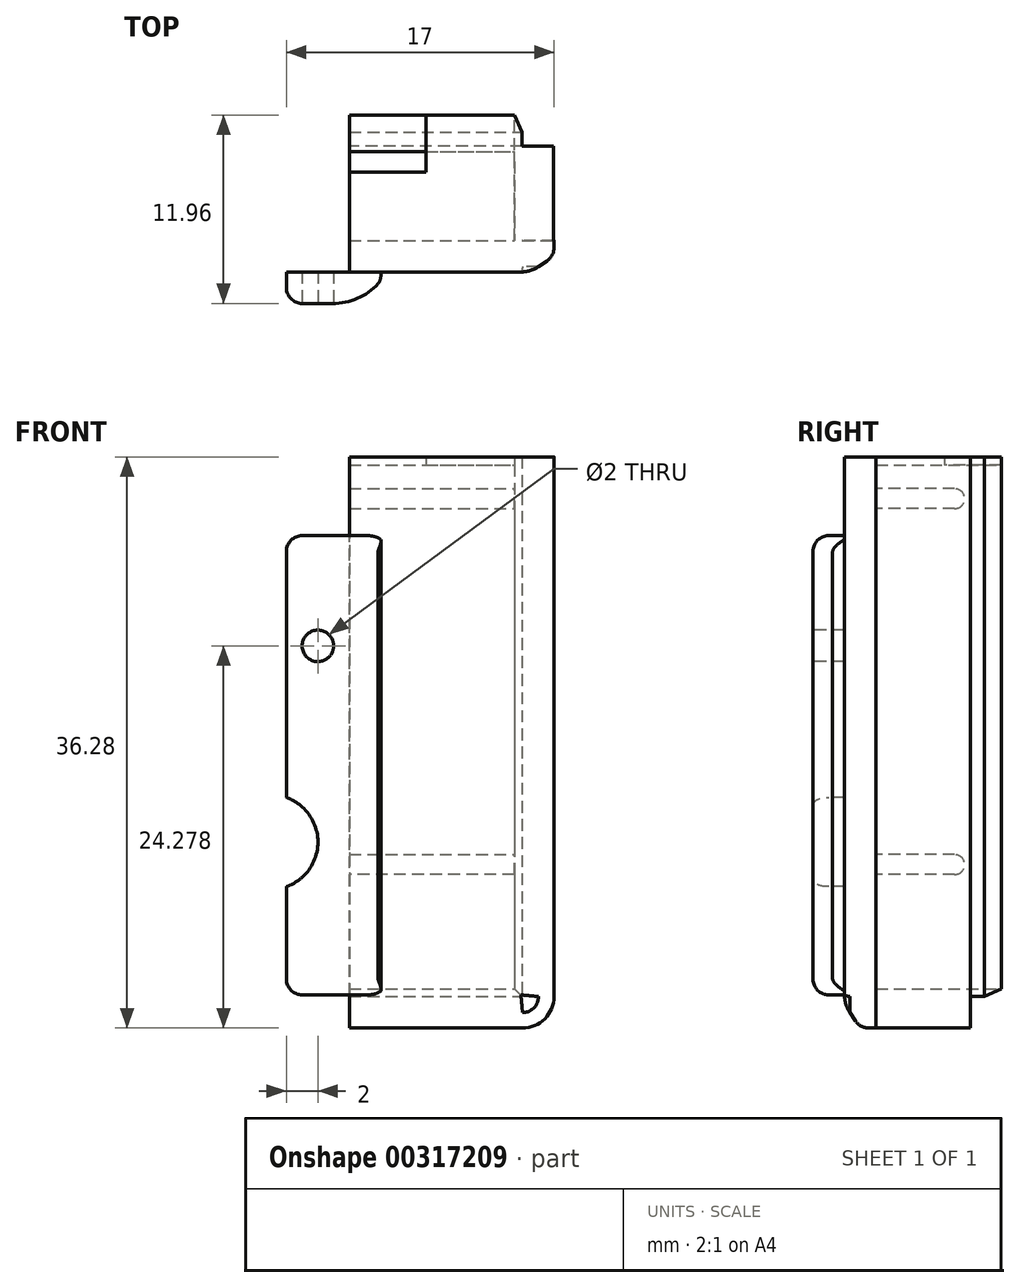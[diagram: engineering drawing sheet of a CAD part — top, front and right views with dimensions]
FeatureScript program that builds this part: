
annotation { "Feature Type Name" : "Feature", "Feature Type Description" : "" }
export const myFeature = defineFeature(function(context is Context, id is Id, definition is map)
    precondition{}
    {
        {
            var Q0;
            Q0=qCreatedBy(makeId("Front.planeOp"),FACE);
            var sketch = newSketch(context, id + "F0", { "sketchPlane" : qUnion([Q0])});
            skLineSegment(sketch, "E0", {"start": v(12.98, 38.01) * mm, "end": v(12.98, 70.29) * mm});
            skLineSegment(sketch, "E1", {"start": v(10.98, 72.29) * mm, "end": v(0, 72.29) * mm});
            skLineSegment(sketch, "E2", {"start": v(0, 72.29) * mm, "end": v(0, 71.79) * mm});
            skLineSegment(sketch, "E3", {"start": v(10.98, 70.29) * mm, "end": v(10.98, 38.01) * mm});
            skPoint(sketch, "E4.visualSharp", {"position": v(12.98, 72.29) * mm});
            skPoint(sketch, "E5.visualSharp", {"position": v(12.98, 0) * mm});
            skPoint(sketch, "E6.start.orphan", {"position": v(0, 2) * mm});
            skLineSegment(sketch, "E7", {"start": v(10.98, 36.01) * mm, "end": v(0, 36.01) * mm});
            skLineSegment(sketch, "E8", {"start": v(0, 36.01) * mm, "end": v(0, 38.01) * mm});
            skLineSegment(sketch, "E9", {"start": v(0, 38.01) * mm, "end": v(10.98, 38.01) * mm});
            skArc(sketch, "E10.filletArc", {"start": v(10.98, 36.01) * mm, "mid": v(12.4, 36.6) * mm, "end": v(12.98, 38.01) * mm});
            skLineSegment(sketch, "E11", {"start": v(12.98, 70.29) * mm, "end": v(12.98, 72.29) * mm});
            skLineSegment(sketch, "E12", {"start": v(12.98, 72.29) * mm, "end": v(10.98, 72.29) * mm});
            skLineSegment(sketch, "E13", {"start": v(0, 71.79) * mm, "end": v(10.98, 71.79) * mm});
            skLineSegment(sketch, "E14", {"start": v(10.98, 71.79) * mm, "end": v(10.98, 70.29) * mm});
            skSolve(sketch);
        }
        {
            var Q0;
            Q0=makeQuery(id+"F0.imprint","IMPRINT",FACE,{"disambiguationData":[TD([[makeQuery(id+"F0.imprint","IMPRINT",EDGE,{"derivedFrom":sQuery(id+"F0.wireOp",EDGE,"E0")}),1.0]])]});
            extrude(context, id + "F1", {"entities" : qUnion([Q0]), "depth" : 6 * mm});
        }
        {
            var Q0;
            Q0=makeQuery(id+"F1.opExtrude","SWEPT_FACE",FACE,{"disambiguationData":[OSD([sQuery(id+"F0.wireOp",EDGE,"E2")])]});
            var sketch = newSketch(context, id + "F2", { "sketchPlane" : qUnion([Q0])});
            skLineSegment(sketch, "E15.bottom", {"start": v(6, 72.29) * mm, "end": v(8, 72.29) * mm});
            skLineSegment(sketch, "E15.left", {"start": v(6, 72.29) * mm, "end": v(6, 36.3) * mm});
            skLineSegment(sketch, "E15.right", {"start": v(8, 72.29) * mm, "end": v(8, 36.3) * mm});
            skLineSegment(sketch, "E16", {"start": v(6, 36.3) * mm, "end": v(6, 36.01) * mm});
            skLineSegment(sketch, "E17", {"start": v(6, 36.01) * mm, "end": v(8, 36.01) * mm});
            skLineSegment(sketch, "E18", {"start": v(8, 36.01) * mm, "end": v(8, 36.3) * mm});
            skSolve(sketch);
        }
        {
            var Q0;
            Q0=qSketchRegion(id+"F2",true);
            extrude(context, id + "F3", {"entities" : qUnion([Q0]), "operationType" : NewBodyOperationType.ADD, "oppositeDirection" : true, "depth" : 13 * mm});
        }
        {
            var Q0;
            Q0=makeQuery(id+"F3.opExtrude","CAP_EDGE",EDGE,{"disambiguationData":[OSD([sQuery(id+"F2.wireOp",EDGE,"E15.top")])],"isStart":false});
            var Q1;
            Q1=makeQuery(id+"F3.opExtrude","CAP_EDGE",EDGE,{"disambiguationData":[OSD([sQuery(id+"F2.wireOp",EDGE,"E17")])],"isStart":false});
            fillet(context, id + "F4", {"entities" : qUnion([Q0, Q1]), "radius" : 2 * mm, "tangentPropagation" : true, "allowEdgeOverflow" : false});
        }
        {
            var Q0;
            Q0=makeQuery(id+"F3.opExtrude","SWEPT_FACE",FACE,{"disambiguationData":[OSD([sQuery(id+"F2.wireOp",EDGE,"E15.right")])]});
            var sketch = newSketch(context, id + "F5", { "sketchPlane" : qUnion([Q0])});
            skLineSegment(sketch, "E19.bottom", {"start": v(2, 67.29) * mm, "end": v(-4, 67.29) * mm});
            skLineSegment(sketch, "E19.top", {"start": v(2, 38.12) * mm, "end": v(-4, 38.12) * mm});
            skLineSegment(sketch, "E19.left", {"start": v(2, 67.29) * mm, "end": v(2, 38.12) * mm});
            skLineSegment(sketch, "E19.right", {"start": v(-4, 67.29) * mm, "end": v(-4, 38.12) * mm});
            skSolve(sketch);
        }
        {
            var Q0;
            Q0=qSketchRegion(id+"F5",true);
            extrude(context, id + "F6", {"entities" : qUnion([Q0]), "operationType" : NewBodyOperationType.ADD, "depth" : 2 * mm});
        }
        {
            var Q0;
            Q0=makeQuery(id+"F6.opExtrude","CAP_EDGE",EDGE,{"disambiguationData":[OSD([sQuery(id+"F5.wireOp",EDGE,"E19.left")])],"isStart":false});
            chamfer(context, id + "F7", {"entities" : qUnion([Q0]), "chamferType" : ChamferType.TWO_OFFSETS, "width1" : 1.5 * mm, "oppositeDirection" : false, "width2" : 1 * mm, "tangentPropagation" : true});
        }
        {
            var Q0;
            {var subQ0=sQuery(id+"F5.wireOp",EDGE,"E19.left");Q0=makeQuery(id+"F7.opChamfer","BLEND_EDGE",EDGE,{"blendedFrom":[makeQuery(id+"F6.opExtrude","CAP_EDGE",EDGE,{"disambiguationData":[OSD([subQ0])],"isStart":false}),makeQuery(id+"F6.opExtrude","SWEPT_FACE",FACE,{"disambiguationData":[OSD([subQ0])]})],"blendedInto":[makeQuery(id+"F6.opExtrude","SWEPT_FACE",FACE,{"disambiguationData":[OSD([subQ0])]})]});}
            fillet(context, id + "F8", {"entities" : qUnion([Q0]), "radius" : 1 * mm, "tangentPropagation" : true, "allowEdgeOverflow" : false});
        }
        {
            var Q0;
            Q0=makeQuery(id+"F6.opExtrude","CAP_FACE",FACE,{"disambiguationData":[OSD([sQuery(id+"F5.wireOp",EDGE,"E19.bottom"),sQuery(id+"F5.wireOp",EDGE,"E19.top"),sQuery(id+"F5.wireOp",EDGE,"E19.left"),sQuery(id+"F5.wireOp",EDGE,"E19.right")])],"isStart":false});
            var sketch = newSketch(context, id + "F9", { "sketchPlane" : qUnion([Q0])});
            skCircle(sketch, "E20", {"center": v(-2, 60.29) * mm, "radius": 1 * mm});
            skSolve(sketch);
        }
        {
            var Q0;
            Q0=qSketchRegion(id+"F9",true);
            extrude(context, id + "F10", {"entities" : qUnion([Q0]), "operationType" : NewBodyOperationType.REMOVE, "oppositeDirection" : true, "depth" : 25 * mm});
        }
        {
            var Q0;
            {var subQ0=sQuery(id+"F5.wireOp",EDGE,"E19.left");Q0=makeQuery(id+"F7.opChamfer","BLEND_EDGE",EDGE,{"blendedFrom":[makeQuery(id+"F6.opExtrude","CAP_EDGE",EDGE,{"disambiguationData":[OSD([subQ0])],"isStart":false}),makeQuery(id+"F6.opExtrude","CAP_FACE",FACE,{"disambiguationData":[OSD([sQuery(id+"F5.wireOp",EDGE,"E19.bottom"),sQuery(id+"F5.wireOp",EDGE,"E19.top"),subQ0,sQuery(id+"F5.wireOp",EDGE,"E19.right")])],"isStart":false})],"blendedInto":[makeQuery(id+"F6.opExtrude","CAP_FACE",FACE,{"disambiguationData":[OSD([sQuery(id+"F5.wireOp",EDGE,"E19.bottom"),sQuery(id+"F5.wireOp",EDGE,"E19.top"),subQ0,sQuery(id+"F5.wireOp",EDGE,"E19.right")])],"isStart":false})]});}
            fillet(context, id + "F11", {"entities" : qUnion([Q0]), "radius" : 4 * mm, "tangentPropagation" : true, "allowEdgeOverflow" : false});
        }
        {
            var Q0;
            Q0=makeQuery(id+"F6.opExtrude","CAP_EDGE",EDGE,{"disambiguationData":[OSD([sQuery(id+"F5.wireOp",EDGE,"E19.top")])],"isStart":false});
            var Q1;
            Q1=makeQuery(id+"F6.opExtrude","CAP_EDGE",EDGE,{"disambiguationData":[OSD([sQuery(id+"F5.wireOp",EDGE,"E19.bottom")])],"isStart":false});
            fillet(context, id + "F12", {"entities" : qUnion([Q0, Q1]), "radius" : 1 * mm, "tangentPropagation" : true, "allowEdgeOverflow" : false});
        }
        {
            var Q0;
            Q0=makeQuery(id+"F6.opExtrude","CAP_EDGE",EDGE,{"disambiguationData":[OSD([sQuery(id+"F5.wireOp",EDGE,"E19.right")])],"isStart":false});
            fillet(context, id + "F13", {"entities" : qUnion([Q0]), "radius" : 1 * mm, "tangentPropagation" : true, "allowEdgeOverflow" : false});
        }
        {
            var Q0;
            Q0=makeQuery(id+"F1.opExtrude","CAP_FACE",FACE,{"disambiguationData":[OSD([sQuery(id+"F0.wireOp",EDGE,"E0"),sQuery(id+"F0.wireOp",EDGE,"E1"),sQuery(id+"F0.wireOp",EDGE,"E2"),sQuery(id+"F0.wireOp",EDGE,"5GWelT8N-WT9G-pHX5-dFQZ-JpsdUA8wokHI"),sQuery(id+"F0.wireOp",EDGE,"E3"),sQuery(id+"F0.wireOp",EDGE,"E4.filletArc"),sQuery(id+"F0.wireOp",EDGE,"SL8cM0Mj-z6Pg-xHqj-tJNP-eVUlfgKiLkpK")])],"isStart":true});
            var sketch = newSketch(context, id + "F14", { "sketchPlane" : qUnion([Q0])});
            skLineSegment(sketch, "E21.left", {"start": v(-10.98, 38.01) * mm, "end": v(-10.98, 38.01) * mm});
            skLineSegment(sketch, "E21.right", {"start": v(-10.48, 70.29) * mm, "end": v(-10.48, 38.51) * mm});
            skLineSegment(sketch, "E22.bottom", {"start": v(-10.98, 72.29) * mm, "end": v(0, 72.29) * mm});
            skLineSegment(sketch, "E22.top", {"start": v(-10.48, 71.79) * mm, "end": v(0, 71.79) * mm});
            skLineSegment(sketch, "E22.left", {"start": v(-10.98, 72.29) * mm, "end": v(-10.98, 71.79) * mm});
            skLineSegment(sketch, "E22.right", {"start": v(0, 72.29) * mm, "end": v(0, 71.79) * mm});
            skLineSegment(sketch, "E23.bottom", {"start": v(-10.98, 72.29) * mm, "end": v(-10.48, 72.29) * mm});
            skLineSegment(sketch, "E23.left", {"start": v(-10.98, 72.29) * mm, "end": v(-10.98, 69.79) * mm});
            skLineSegment(sketch, "E23.right", {"start": v(-10.48, 71.79) * mm, "end": v(-10.48, 38.01) * mm});
            skLineSegment(sketch, "E24.bottom", {"start": v(0, 38.01) * mm, "end": v(-10.98, 38.01) * mm});
            skLineSegment(sketch, "E24.top", {"start": v(0, 38.51) * mm, "end": v(-10.48, 38.51) * mm});
            skLineSegment(sketch, "E24.left", {"start": v(0, 38.01) * mm, "end": v(0, 38.51) * mm});
            skLineSegment(sketch, "E24.right", {"start": v(-10.98, 38.01) * mm, "end": v(-10.98, 38.51) * mm});
            skLineSegment(sketch, "E25", {"start": v(-10.98, 38.51) * mm, "end": v(-10.98, 69.79) * mm});
            skSolve(sketch);
        }
        {
            var Q0;
            Q0=qSketchRegion(id+"F14",true);
            extrude(context, id + "F15", {"entities" : qUnion([Q0]), "operationType" : NewBodyOperationType.ADD, "oppositeDirection" : true, "depth" : 6.1 * mm, "hasSecondDirection" : true, "secondDirectionOppositeDirection" : false, "secondDirectionDepth" : 1.97 * mm});
        }
        {
            var Q0;
            Q0=makeQuery(id+"F15.opExtrude","CAP_EDGE",EDGE,{"disambiguationData":[OSD([sQuery(id+"F14.wireOp",EDGE,"E23.left"),sQuery(id+"F14.wireOp",EDGE,"E24.right"),sQuery(id+"F14.wireOp",EDGE,"E25")])],"isStart":true});
            var Q1;
            Q1=makeQuery(id+"F15.opExtrude","CAP_EDGE",EDGE,{"disambiguationData":[OSD([sQuery(id+"F14.wireOp",EDGE,"E24.bottom")])],"isStart":true});
            chamfer(context, id + "F16", {"entities" : qUnion([Q0, Q1]), "chamferType" : ChamferType.OFFSET_ANGLE, "width" : 0.5 * mm, "oppositeDirection" : false, "angle" : 65 * degree, "tangentPropagation" : true});
        }
        {
            var Q0;
            {var subQ1=sQuery(id+"F2.wireOp",EDGE,"E15.left");Q0=makeQuery(id+"F3.boolean.opBoolean","SPLIT",FACE,{"disambiguationData":[TD([makeQuery(id+"F1.opExtrude","SWEPT_FACE",FACE,{"disambiguationData":[OSD([sQuery(id+"F0.wireOp",EDGE,"E2")])]})])],"derivedFrom":makeQuery(id+"F3.opExtrude","SWEPT_FACE",FACE,{"disambiguationData":[OSD([subQ1])]})});}
            var sketch = newSketch(context, id + "F17", { "sketchPlane" : qUnion([Q0])});
            skLineSegment(sketch, "E26", {"start": v(-10.48, 45.76) * mm, "end": v(-7.39, 45.76) * mm});
            skLineSegment(sketch, "E27", {"start": v(-10.48, 47.03) * mm, "end": v(-7.39, 47.03) * mm});
            skLineSegment(sketch, "E28", {"start": v(-7.39, 45.76) * mm, "end": v(0, 45.76) * mm});
            skLineSegment(sketch, "E29", {"start": v(0, 45.76) * mm, "end": v(0, 47.03) * mm});
            skLineSegment(sketch, "E30", {"start": v(0, 47.03) * mm, "end": v(-7.39, 47.03) * mm});
            skLineSegment(sketch, "E31.bottom", {"start": v(0, 70.28) * mm, "end": v(-10.48, 70.28) * mm});
            skLineSegment(sketch, "E31.top", {"start": v(0, 69) * mm, "end": v(-10.48, 69) * mm});
            skLineSegment(sketch, "E31.left", {"start": v(0, 70.28) * mm, "end": v(0, 69) * mm});
            skLineSegment(sketch, "E31.right", {"start": v(-10.48, 70.28) * mm, "end": v(-10.48, 69) * mm});
            skSolve(sketch);
        }
        {
            var Q0;
            {var subQ0=sQuery(id+"F17.wireOp",EDGE,"E26");Q0=makeQuery(id+"F17.imprint","IMPRINT",FACE,{"disambiguationData":[TD([[makeQuery(id+"F17.imprint","IMPRINT",EDGE,{"derivedFrom":subQ0}),1.0]])]});}
            var Q1;
            Q1=makeQuery(id+"F17.imprint","IMPRINT",FACE,{"disambiguationData":[TD([[makeQuery(id+"F17.imprint","IMPRINT",EDGE,{"derivedFrom":sQuery(id+"F17.wireOp",EDGE,"E31.bottom")}),1.0]])]});
            extrude(context, id + "F18", {"entities" : qUnion([Q0, Q1]), "operationType" : NewBodyOperationType.ADD, "depth" : 5.63 * mm});
        }
        {
            var Q0;
            Q0=makeQuery(id+"F18.opExtrude","CAP_EDGE",EDGE,{"disambiguationData":[OSD([sQuery(id+"F17.wireOp",EDGE,"E26")])],"isStart":false});
            var Q1;
            Q1=makeQuery(id+"F18.opExtrude","CAP_EDGE",EDGE,{"disambiguationData":[OSD([sQuery(id+"F17.wireOp",EDGE,"E27")])],"isStart":false});
            var Q2;
            Q2=makeQuery(id+"F18.opExtrude","CAP_EDGE",EDGE,{"disambiguationData":[OSD([sQuery(id+"F17.wireOp",EDGE,"E31.top")])],"isStart":false});
            var Q3;
            Q3=makeQuery(id+"F18.opExtrude","CAP_EDGE",EDGE,{"disambiguationData":[OSD([sQuery(id+"F17.wireOp",EDGE,"E31.bottom")])],"isStart":false});
            fillet(context, id + "F19", {"entities" : qUnion([Q0, Q1, Q2, Q3]), "radius" : 0.64 * mm, "tangentPropagation" : true, "allowEdgeOverflow" : false});
        }
        {
            var Q0;
            Q0=makeQuery(id+"F3.opExtrude","SWEPT_EDGE",EDGE,{"disambiguationData":[OSD([sQuery(id+"F2.wireOp",EDGE,"E17"),sQuery(id+"F2.wireOp",EDGE,"E18")])]});
            chamfer(context, id + "F20", {"entities" : qUnion([Q0]), "chamferType" : ChamferType.TWO_OFFSETS, "width1" : 1 * mm, "oppositeDirection" : false, "width2" : 1.5 * mm, "tangentPropagation" : true});
        }
        {
            var Q0;
            {var subQ0=sQuery(id+"F2.wireOp",EDGE,"E18");Q0=makeQuery(id+"F20.opChamfer","BLEND_EDGE",EDGE,{"blendedFrom":[makeQuery(id+"F3.opExtrude","SWEPT_EDGE",EDGE,{"disambiguationData":[OSD([sQuery(id+"F2.wireOp",EDGE,"E17"),subQ0])]}),makeQuery(id+"F3.opExtrude","SWEPT_FACE",FACE,{"disambiguationData":[OSD([sQuery(id+"F2.wireOp",EDGE,"E15.right"),subQ0])]})],"blendedInto":[makeQuery(id+"F3.opExtrude","SWEPT_FACE",FACE,{"disambiguationData":[OSD([sQuery(id+"F2.wireOp",EDGE,"E15.right"),subQ0])]})]});}
            fillet(context, id + "F21", {"entities" : qUnion([Q0]), "radius" : 2 * mm, "tangentPropagation" : true, "allowEdgeOverflow" : false});
        }
        {
            var Q0;
            {var subQ0=sQuery(id+"F2.wireOp",EDGE,"E17");Q0=makeQuery(id+"F20.opChamfer","BLEND_EDGE",EDGE,{"blendedFrom":[makeQuery(id+"F3.opExtrude","SWEPT_EDGE",EDGE,{"disambiguationData":[OSD([subQ0,sQuery(id+"F2.wireOp",EDGE,"E18")])]}),makeQuery(id+"F3.boolean.opBoolean","MERGE",FACE,{"derivedFrom":[makeQuery(id+"F1.opExtrude","SWEPT_FACE",FACE,{"disambiguationData":[OSD([sQuery(id+"F0.wireOp",EDGE,"E7")])]}),makeQuery(id+"F3.opExtrude","SWEPT_FACE",FACE,{"disambiguationData":[OSD([subQ0])]})]})],"blendedInto":[makeQuery(id+"F3.boolean.opBoolean","MERGE",FACE,{"derivedFrom":[makeQuery(id+"F1.opExtrude","SWEPT_FACE",FACE,{"disambiguationData":[OSD([sQuery(id+"F0.wireOp",EDGE,"E7")])]}),makeQuery(id+"F3.opExtrude","SWEPT_FACE",FACE,{"disambiguationData":[OSD([subQ0])]})]})]});}
            fillet(context, id + "F22", {"entities" : qUnion([Q0]), "radius" : 1 * mm, "tangentPropagation" : true, "allowEdgeOverflow" : false});
        }
        {
            var Q0;
            Q0=makeQuery(id+"F15.boolean.opBoolean","MERGE",FACE,{"derivedFrom":[makeQuery(id+"F1.opExtrude","SWEPT_FACE",FACE,{"disambiguationData":[OSD([sQuery(id+"F0.wireOp",EDGE,"E13")])]}),makeQuery(id+"F15.opExtrude","SWEPT_FACE",FACE,{"disambiguationData":[OSD([sQuery(id+"F14.wireOp",EDGE,"E22.top")])]})]});
            var sketch = newSketch(context, id + "F23", { "sketchPlane" : qUnion([Q0])});
            skLineSegment(sketch, "E32.bottom", {"start": v(0, -1.97) * mm, "end": v(4.88, -1.97) * mm});
            skLineSegment(sketch, "E32.top", {"start": v(0, 1.64) * mm, "end": v(4.88, 1.64) * mm});
            skLineSegment(sketch, "E32.left", {"start": v(0, -1.97) * mm, "end": v(0, 1.64) * mm});
            skLineSegment(sketch, "E32.right", {"start": v(4.88, -1.97) * mm, "end": v(4.88, 1.64) * mm});
            skSolve(sketch);
        }
        {
            var Q0;
            Q0=qSketchRegion(id+"F23",true);
            extrude(context, id + "F24", {"entities" : qUnion([Q0]), "operationType" : NewBodyOperationType.REMOVE, "oppositeDirection" : true, "depth" : 25 * mm});
        }
        {
            var Q0;
            Q0=makeQuery(id+"F13.opFillet","SPLIT",FACE,{"disambiguationData":[OD(1.0)],"derivedFrom":makeQuery(id+"F6.opExtrude","CAP_FACE",FACE,{"disambiguationData":[OSD([sQuery(id+"F5.wireOp",EDGE,"E19.bottom"),sQuery(id+"F5.wireOp",EDGE,"E19.top"),sQuery(id+"F5.wireOp",EDGE,"E19.left"),sQuery(id+"F5.wireOp",EDGE,"E19.right")])],"isStart":false})});
            var sketch = newSketch(context, id + "F25", { "sketchPlane" : qUnion([Q0])});
            skCircle(sketch, "E33", {"center": v(-5, 47.82) * mm, "radius": 3 * mm});
            skSolve(sketch);
        }
        {
            var Q0;
            Q0=qSketchRegion(id+"F25",true);
            extrude(context, id + "F26", {"entities" : qUnion([Q0]), "operationType" : NewBodyOperationType.REMOVE, "oppositeDirection" : true, "depth" : 25 * mm});
        }
    });
